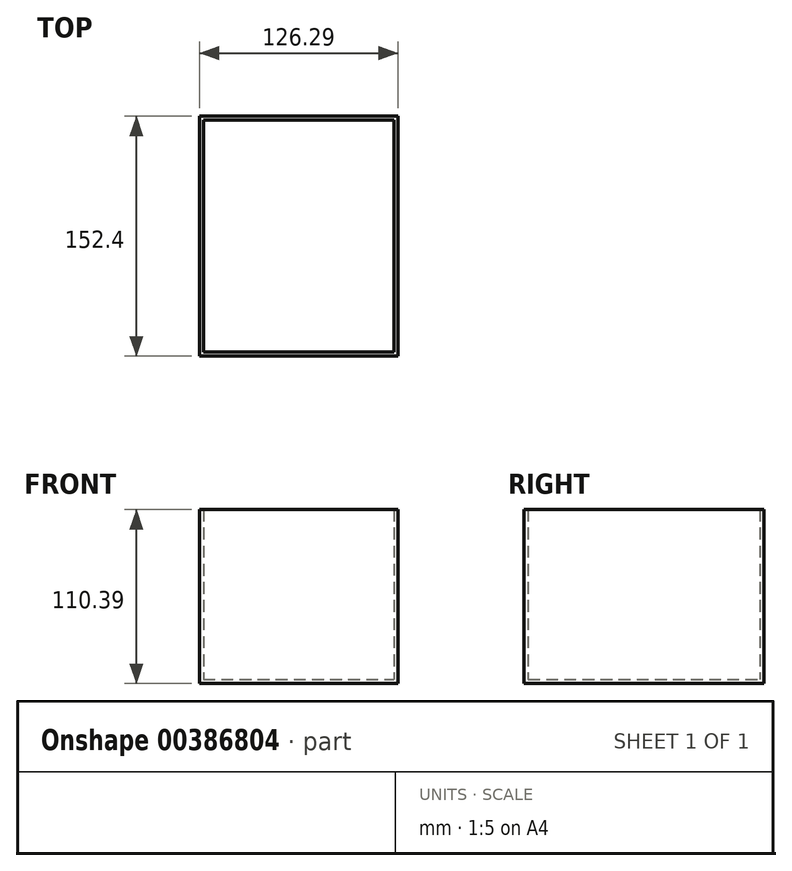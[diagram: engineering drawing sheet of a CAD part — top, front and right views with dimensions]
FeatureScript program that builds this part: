
annotation { "Feature Type Name" : "Feature", "Feature Type Description" : "" }
export const myFeature = defineFeature(function(context is Context, id is Id, definition is map)
    precondition{}
    {
        {
            var Q0;
            Q0=qCreatedBy(makeId("Front.planeOp"),FACE);
            var sketch = newSketch(context, id + "F0", { "sketchPlane" : qUnion([Q0])});
            skLineSegment(sketch, "E0", {"start": v(-49.65, 54.37) * mm, "end": v(-49.65, -56.02) * mm});
            skLineSegment(sketch, "E1", {"start": v(-49.65, 54.37) * mm, "end": v(76.37, 54.37) * mm});
            skLineSegment(sketch, "E2", {"start": v(-49.65, -56.02) * mm, "end": v(76.64, -56.02) * mm});
            skLineSegment(sketch, "E3", {"start": v(76.37, 54.37) * mm, "end": v(76.64, -56.02) * mm});
            skSolve(sketch);
        }
        {
            var Q0;
            Q0=makeQuery(id+"F0.imprint","IMPRINT",FACE,{"disambiguationData":[TD([[makeQuery(id+"F0.imprint","IMPRINT",EDGE,{"derivedFrom":sQuery(id+"F0.wireOp",EDGE,"E0")}),1.0]])]});
            extrude(context, id + "F1", {"entities" : qUnion([Q0]), "depth" : 152.4 * mm});
        }
        {
            var Q0;
            Q0=makeQuery(id+"F1.opExtrude","SWEPT_FACE",FACE,{"disambiguationData":[OSD([sQuery(id+"F0.wireOp",EDGE,"E1")])]});
            shell(context, id + "F2", {"entities" : qUnion([Q0]), "thickness" : 2.54 * mm});
        }
    });
